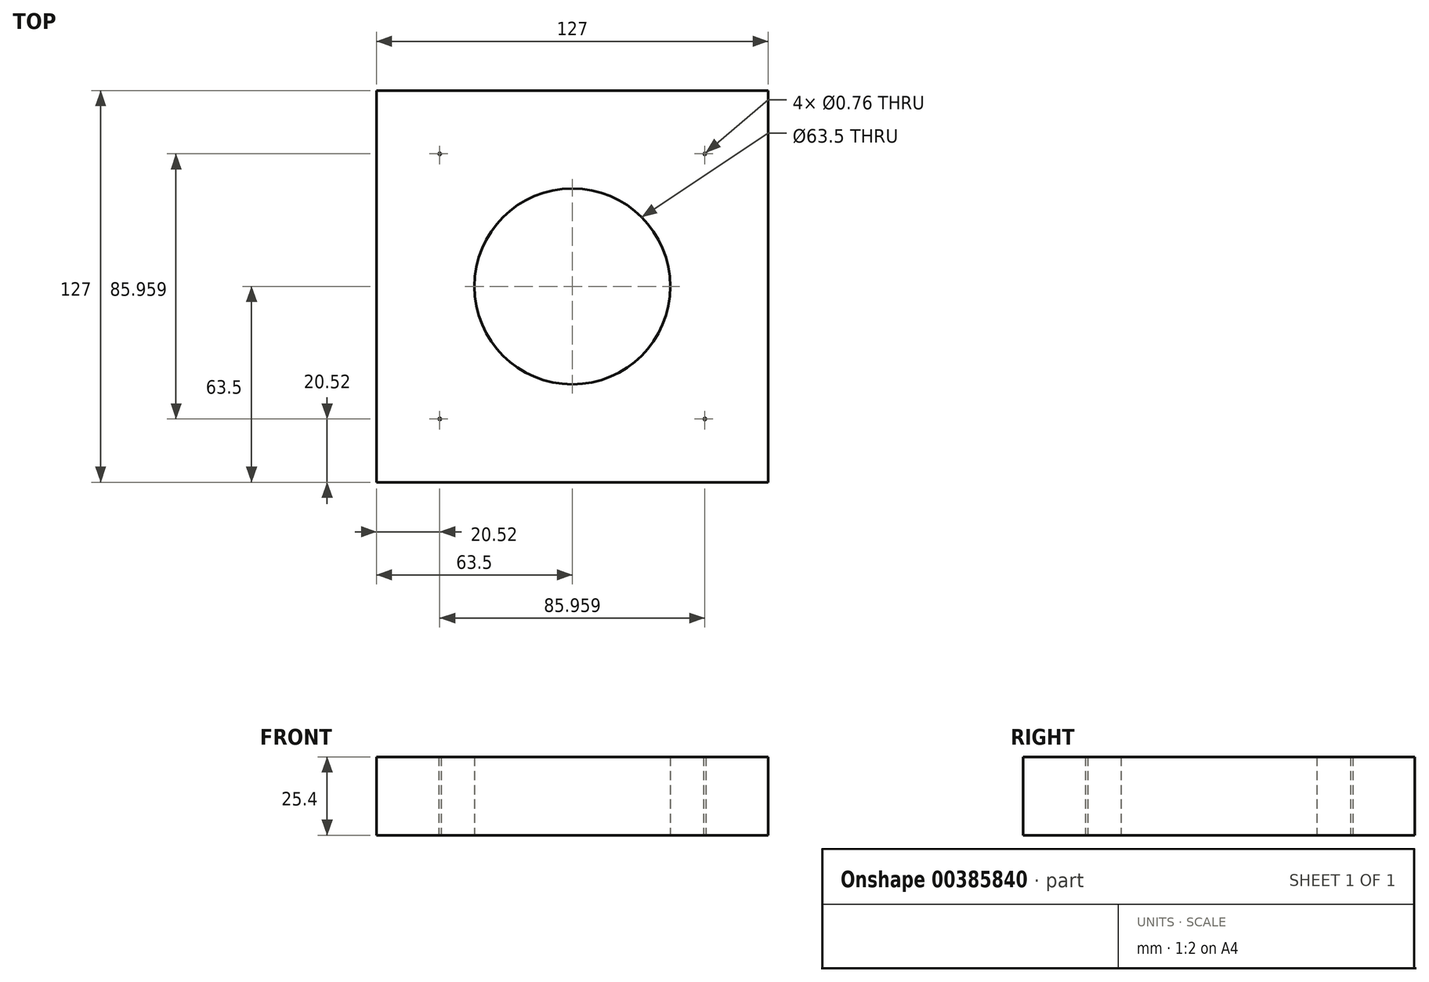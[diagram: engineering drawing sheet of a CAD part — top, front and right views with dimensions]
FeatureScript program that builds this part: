
annotation { "Feature Type Name" : "Feature", "Feature Type Description" : "" }
export const myFeature = defineFeature(function(context is Context, id is Id, definition is map)
    precondition{}
    {
        {
            var Q0;
            Q0=qCreatedBy(makeId("Top.planeOp"),FACE);
            var sketch = newSketch(context, id + "F0", { "sketchPlane" : qUnion([Q0])});
            skLineSegment(sketch, "E0.bottom", {"start": v(-63.5, 63.5) * mm, "end": v(63.5, 63.5) * mm});
            skLineSegment(sketch, "E0.top", {"start": v(-63.5, -63.5) * mm, "end": v(63.5, -63.5) * mm});
            skLineSegment(sketch, "E0.left", {"start": v(-63.5, 63.5) * mm, "end": v(-63.5, -63.5) * mm});
            skLineSegment(sketch, "E0.right", {"start": v(63.5, 63.5) * mm, "end": v(63.5, -63.5) * mm});
            skPoint(sketch, "E0.middle", {"position": v(0, 0) * mm});
            skCircle(sketch, "E1", {"center": v(-42.98, 42.98) * mm, "radius": 0.38 * mm});
            skCircle(sketch, "E2", {"center": v(42.98, 42.98) * mm, "radius": 0.38 * mm});
            skCircle(sketch, "E3", {"center": v(42.98, -42.98) * mm, "radius": 0.38 * mm});
            skCircle(sketch, "E4", {"center": v(-42.98, -42.98) * mm, "radius": 0.38 * mm});
            skCircle(sketch, "E5", {"center": v(0, 0) * mm, "radius": 0.38 * mm});
            skCircle(sketch, "E6", {"center": v(0, 0) * mm, "radius": 31.75 * mm});
            skCircle(sketch, "E7", {"center": v(0, 0) * mm, "radius": 25.04 * mm});
            skSolve(sketch);
        }
        {
            var Q0;
            Q0=makeQuery(id+"F0.imprint","IMPRINT",FACE,{"disambiguationData":[TD([[makeQuery(id+"F0.imprint","IMPRINT",EDGE,{"derivedFrom":sQuery(id+"F0.wireOp",EDGE,"E0.bottom")}),-1.0]])]});
            extrude(context, id + "F1", {"entities" : qUnion([Q0]), "depth" : 25.4 * mm});
        }
    });
